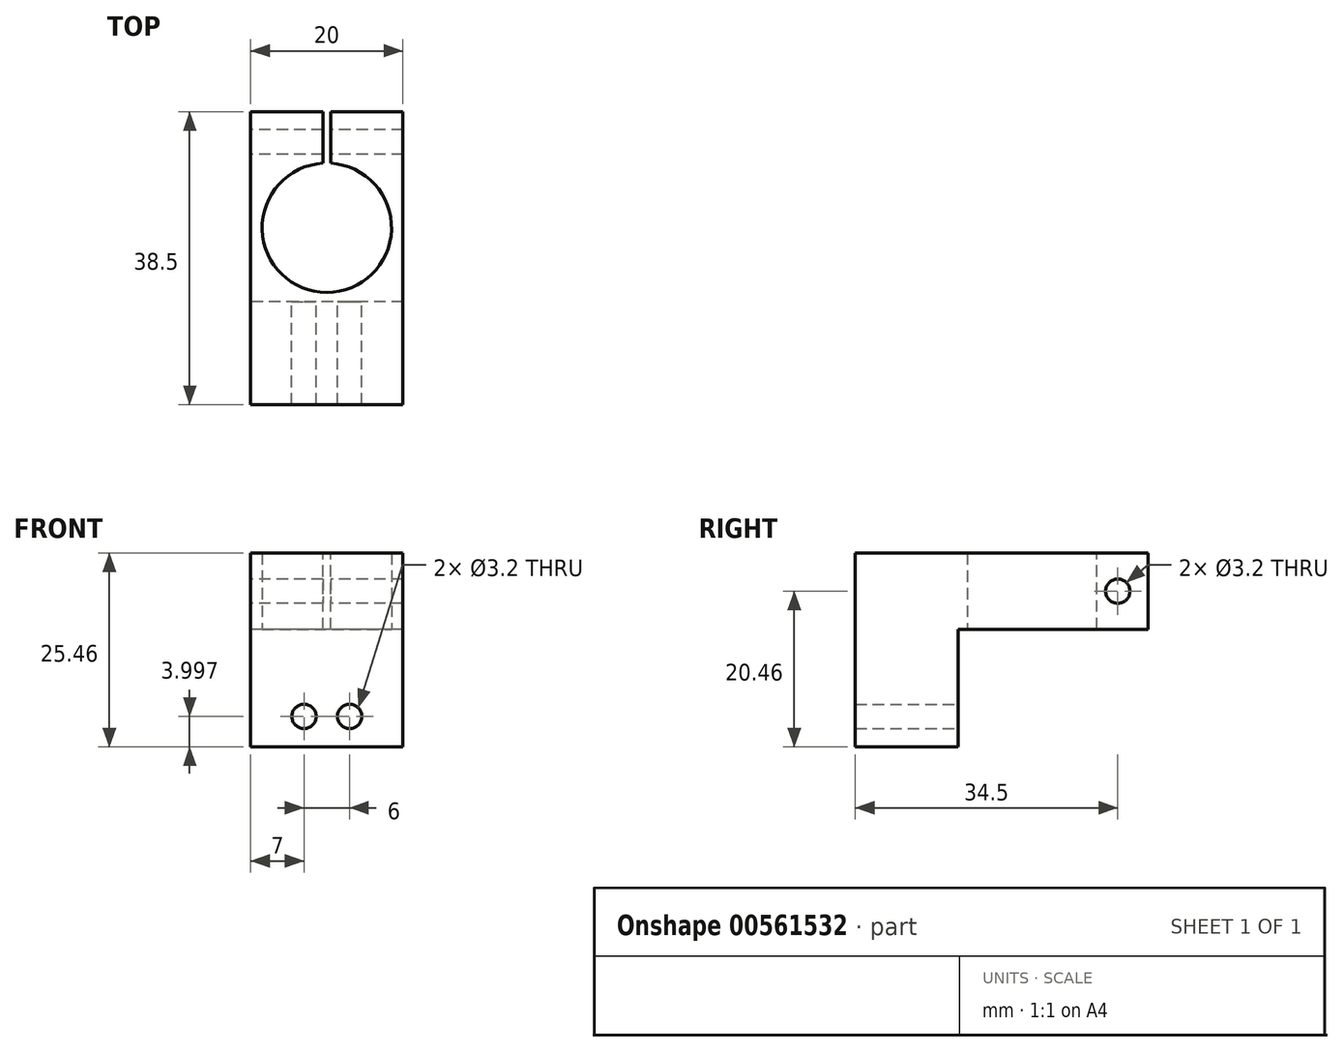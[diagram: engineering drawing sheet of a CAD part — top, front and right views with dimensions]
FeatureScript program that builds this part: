
annotation { "Feature Type Name" : "Feature", "Feature Type Description" : "" }
export const myFeature = defineFeature(function(context is Context, id is Id, definition is map)
    precondition{}
    {
        {
            var Q0;
            Q0=qCreatedBy(makeId("Top.planeOp"),FACE);
            var sketch = newSketch(context, id + "F0", { "sketchPlane" : qUnion([Q0])});
            skLineSegment(sketch, "E0.bottom", {"start": v(10, -12.5) * mm, "end": v(-10, -12.5) * mm});
            skLineSegment(sketch, "E0.top", {"start": v(10, 12.5) * mm, "end": v(-10, 12.5) * mm});
            skLineSegment(sketch, "E0.left", {"start": v(10, -12.5) * mm, "end": v(10, 12.5) * mm});
            skLineSegment(sketch, "E0.right", {"start": v(-10, -12.5) * mm, "end": v(-10, 12.5) * mm});
            skPoint(sketch, "E0.middle", {"position": v(0, 0) * mm});
            skCircle(sketch, "E1", {"center": v(0, -2.76) * mm, "radius": 8.5 * mm});
            skSolve(sketch);
        }
        {
            var Q0;
            Q0=qSketchRegion(id+"F0",true);
            extrude(context, id + "F1", {"entities" : qUnion([Q0]), "depth" : 10 * mm, "offsetDistance" : 25 * mm});
        }
        {
            var Q0;
            Q0=makeQuery(id+"F1.opExtrude","CAP_FACE",FACE,{"disambiguationData":[OSD([sQuery(id+"F0.wireOp",EDGE,"E0.bottom"),sQuery(id+"F0.wireOp",EDGE,"E0.top"),sQuery(id+"F0.wireOp",EDGE,"E0.left"),sQuery(id+"F0.wireOp",EDGE,"E0.right"),sQuery(id+"F0.wireOp",EDGE,"E1")])],"isStart":false});
            var sketch = newSketch(context, id + "F2", { "sketchPlane" : qUnion([Q0])});
            skLineSegment(sketch, "E2.bottom", {"start": v(-0.5, 12.5) * mm, "end": v(0.5, 12.5) * mm});
            skLineSegment(sketch, "E2.top", {"start": v(-0.5, 5.72) * mm, "end": v(0.5, 5.72) * mm});
            skLineSegment(sketch, "E2.left", {"start": v(-0.5, 12.5) * mm, "end": v(-0.5, 5.72) * mm});
            skLineSegment(sketch, "E2.right", {"start": v(0.5, 12.5) * mm, "end": v(0.5, 5.72) * mm});
            skSolve(sketch);
        }
        {
            var Q0;
            Q0=qSketchRegion(id+"F2",true);
            extrude(context, id + "F3", {"entities" : qUnion([Q0]), "operationType" : NewBodyOperationType.REMOVE, "oppositeDirection" : true, "depth" : 10 * mm, "offsetDistance" : 25 * mm});
        }
        {
            var Q0;
            Q0=makeQuery(id+"F1.opExtrude","SWEPT_FACE",FACE,{"disambiguationData":[OSD([sQuery(id+"F0.wireOp",EDGE,"E0.right")])]});
            var sketch = newSketch(context, id + "F4", { "sketchPlane" : qUnion([Q0])});
            skCircle(sketch, "E3", {"center": v(-8.5, 5) * mm, "radius": 1.6 * mm});
            skSolve(sketch);
        }
        {
            var Q0;
            Q0=qSketchRegion(id+"F4",true);
            extrude(context, id + "F5", {"entities" : qUnion([Q0]), "operationType" : NewBodyOperationType.REMOVE, "oppositeDirection" : true, "depth" : 20 * mm, "offsetDistance" : 25 * mm});
        }
        {
            var Q0;
            Q0=makeQuery(id+"F1.opExtrude","SWEPT_FACE",FACE,{"disambiguationData":[OSD([sQuery(id+"F0.wireOp",EDGE,"E0.bottom")])]});
            var sketch = newSketch(context, id + "F6", { "sketchPlane" : qUnion([Q0])});
            skLineSegment(sketch, "E4.bottom", {"start": v(10, 10) * mm, "end": v(-10, 10) * mm});
            skLineSegment(sketch, "E4.top", {"start": v(10, -0.46) * mm, "end": v(-10, -0.46) * mm});
            skLineSegment(sketch, "E4.left", {"start": v(10, 10) * mm, "end": v(10, -0.46) * mm});
            skLineSegment(sketch, "E4.right", {"start": v(-10, 10) * mm, "end": v(-10, -0.46) * mm});
            skPoint(sketch, "E4.middle", {"position": v(0, 4.77) * mm});
            skSolve(sketch);
        }
        {
            var Q0;
            Q0=qSketchRegion(id+"F6",true);
            extrude(context, id + "F7", {"entities" : qUnion([Q0]), "operationType" : NewBodyOperationType.ADD, "depth" : 13.5 * mm, "offsetDistance" : 25 * mm});
        }
        {
            var Q0;
            Q0=makeQuery(id+"F7.opExtrude","SWEPT_FACE",FACE,{"disambiguationData":[OSD([sQuery(id+"F6.wireOp",EDGE,"E4.top")])]});
            var sketch = newSketch(context, id + "F8", { "sketchPlane" : qUnion([Q0])});
            skLineSegment(sketch, "E5.bottom", {"start": v(-10, 12.5) * mm, "end": v(10, 12.5) * mm});
            skLineSegment(sketch, "E5.top", {"start": v(-10, 26) * mm, "end": v(10, 26) * mm});
            skLineSegment(sketch, "E5.left", {"start": v(-10, 12.5) * mm, "end": v(-10, 26) * mm});
            skLineSegment(sketch, "E5.right", {"start": v(10, 12.5) * mm, "end": v(10, 26) * mm});
            skPoint(sketch, "E5.middle", {"position": v(0, 19.25) * mm});
            skPoint(sketch, "E5.middle.positionSnap0", {"position": v(10, 19.25) * mm});
            skPoint(sketch, "E5.centerSnap0", {"position": v(10, 19.25) * mm});
            skSolve(sketch);
        }
        {
            var Q0;
            Q0=qSketchRegion(id+"F8",true);
            extrude(context, id + "F9", {"entities" : qUnion([Q0]), "operationType" : NewBodyOperationType.ADD, "depth" : 15 * mm, "offsetDistance" : 25 * mm});
        }
        {
            var Q0;
            Q0=makeQuery(id+"F9.boolean.opBoolean","MERGE",FACE,{"derivedFrom":[makeQuery(id+"F7.opExtrude","CAP_FACE",FACE,{"disambiguationData":[OSD([sQuery(id+"F6.wireOp",EDGE,"E4.bottom"),sQuery(id+"F6.wireOp",EDGE,"E4.top"),sQuery(id+"F6.wireOp",EDGE,"E4.left"),sQuery(id+"F6.wireOp",EDGE,"E4.right")])],"isStart":true}),makeQuery(id+"F9.opExtrude","SWEPT_FACE",FACE,{"disambiguationData":[OSD([sQuery(id+"F8.wireOp",EDGE,"E5.bottom")])]})]});
            var sketch = newSketch(context, id + "F10", { "sketchPlane" : qUnion([Q0])});
            skCircle(sketch, "E6", {"center": v(-3, -11.46) * mm, "radius": 1.6 * mm});
            skCircle(sketch, "E7", {"center": v(3, -11.46) * mm, "radius": 1.6 * mm});
            skSolve(sketch);
        }
        {
            var Q0;
            Q0=qSketchRegion(id+"F10",true);
            extrude(context, id + "F11", {"entities" : qUnion([Q0]), "operationType" : NewBodyOperationType.REMOVE, "oppositeDirection" : true, "depth" : 14 * mm, "offsetDistance" : 25 * mm});
        }
    });
